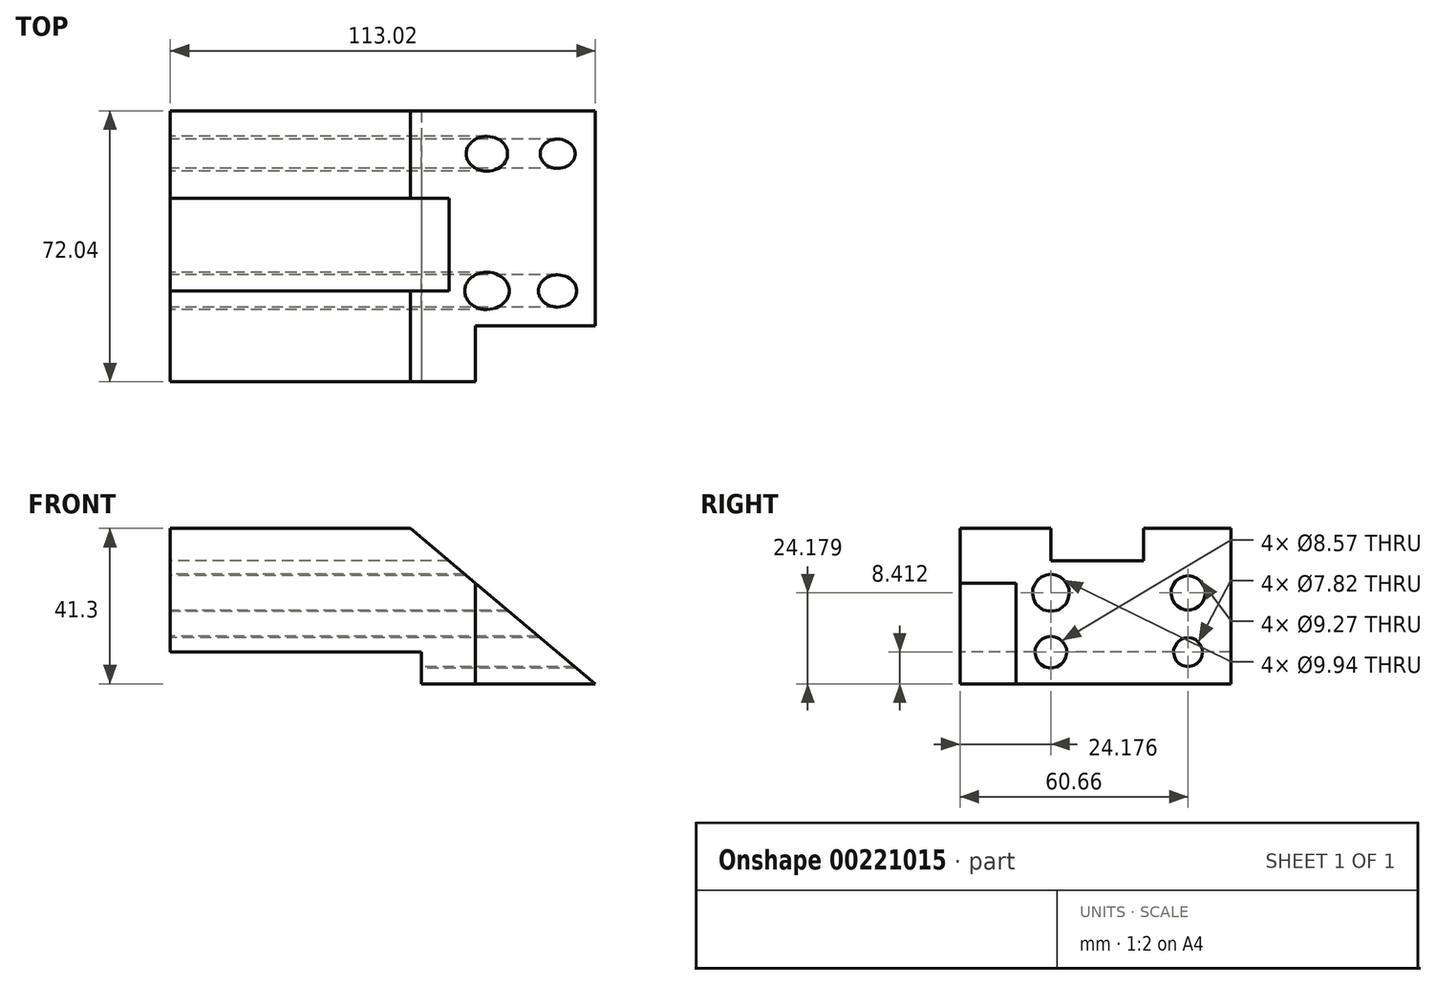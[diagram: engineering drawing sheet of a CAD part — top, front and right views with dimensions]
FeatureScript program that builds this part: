
annotation { "Feature Type Name" : "Feature", "Feature Type Description" : "" }
export const myFeature = defineFeature(function(context is Context, id is Id, definition is map)
    precondition{}
    {
        {
            var Q0;
            Q0=qCreatedBy(makeId("Top.planeOp"),FACE);
            var sketch = newSketch(context, id + "F0", { "sketchPlane" : qUnion([Q0])});
            skLineSegment(sketch, "E0.bottom", {"start": v(57.3, -36.02) * mm, "end": v(-57.3, -36.02) * mm});
            skLineSegment(sketch, "E0.top", {"start": v(57.3, 36.02) * mm, "end": v(-57.3, 36.02) * mm});
            skLineSegment(sketch, "E0.left", {"start": v(57.3, -36.02) * mm, "end": v(57.3, 36.02) * mm});
            skLineSegment(sketch, "E0.right", {"start": v(-57.3, -36.02) * mm, "end": v(-57.3, 36.02) * mm});
            skPoint(sketch, "E0.middle", {"position": v(0, 0) * mm});
            skSolve(sketch);
        }
        {
            var Q0;
            Q0 = qSketchRegion(id + "F0", true);
            extrude(context, id + "F1", {"entities" : qUnion([Q0]), "depth" : 41.3 * mm});
        }
        {
            var Q0;
            Q0=makeQuery(id+"F1.opExtrude","SWEPT_FACE",FACE,{"disambiguationData":[OSD([sQuery(id+"F0.wireOp",EDGE,"E0.bottom")])]});
            var sketch = newSketch(context, id + "F2", { "sketchPlane" : qUnion([Q0])});
            skLineSegment(sketch, "E1.bottom", {"start": v(-57.3, 0) * mm, "end": v(-57.3, 0) * mm});
            skLineSegment(sketch, "E1.top", {"start": v(-57.3, 0) * mm, "end": v(-57.3, 0) * mm});
            skLineSegment(sketch, "E1.left", {"start": v(-57.3, 0) * mm, "end": v(-57.3, 0) * mm});
            skLineSegment(sketch, "E1.right", {"start": v(-57.3, 0) * mm, "end": v(-57.3, 0) * mm});
            skLineSegment(sketch, "E2.bottom", {"start": v(-57.3, 0) * mm, "end": v(9.51, 0) * mm});
            skLineSegment(sketch, "E2.top", {"start": v(-57.3, 8.41) * mm, "end": v(9.51, 8.41) * mm});
            skLineSegment(sketch, "E2.left", {"start": v(-57.3, 0) * mm, "end": v(-57.3, 8.41) * mm});
            skLineSegment(sketch, "E2.right", {"start": v(9.51, 0) * mm, "end": v(9.51, 8.41) * mm});
            skSolve(sketch);
        }
        {
            var Q0;
            Q0 = qSketchRegion(id + "F2", true);
            var Q1;
            Q1=makeQuery(id+"F2.imprint","IMPRINT",FACE,{"disambiguationData":[TD([[makeQuery(id+"F2.imprint","IMPRINT",EDGE,{"derivedFrom":sQuery(id+"F2.wireOp",EDGE,"E2.bottom")}),-1.0]])]});
            extrude(context, id + "F6", {"entities" : qUnion([Q0, Q1]), "operationType" : NewBodyOperationType.REMOVE, "endBound" : BoundingType.THROUGH_ALL, "oppositeDirection" : true, "depth" : 25.4 * mm});
        }
        {
            var Q0;
            Q0=makeQuery(id+"F1.opExtrude","CAP_EDGE",EDGE,{"disambiguationData":[OSD([sQuery(id+"F0.wireOp",EDGE,"E0.left")])],"isStart":false});
            chamfer(context, id + "F7", {"entities" : qUnion([Q0]), "chamferType" : ChamferType.OFFSET_ANGLE, "width" : 50.8 * mm, "oppositeDirection" : false, "angle" : 40 * degree, "tangentPropagation" : true});
        }
        {
            var Q0;
            Q0=makeQuery(id+"F1.opExtrude","CAP_FACE",FACE,{"disambiguationData":[OSD([sQuery(id+"F0.wireOp",EDGE,"E0.bottom"),sQuery(id+"F0.wireOp",EDGE,"E0.top"),sQuery(id+"F0.wireOp",EDGE,"E0.left"),sQuery(id+"F0.wireOp",EDGE,"E0.right")])],"isStart":true});
            var sketch = newSketch(context, id + "F3", { "sketchPlane" : qUnion([Q0])});
            skLineSegment(sketch, "E3.bottom", {"start": v(55.72, 36.02) * mm, "end": v(23.82, 36.02) * mm});
            skLineSegment(sketch, "E3.top", {"start": v(55.72, 21.18) * mm, "end": v(23.82, 21.18) * mm});
            skLineSegment(sketch, "E3.left", {"start": v(55.72, 36.02) * mm, "end": v(55.72, 21.18) * mm});
            skLineSegment(sketch, "E3.right", {"start": v(23.82, 36.02) * mm, "end": v(23.82, 21.18) * mm});
            skSolve(sketch);
        }
        {
            var Q0;
            Q0=makeQuery(id+"F3.imprint","IMPRINT",FACE,{"disambiguationData":[TD([[makeQuery(id+"F3.imprint","IMPRINT",EDGE,{"derivedFrom":sQuery(id+"F3.wireOp",EDGE,"E3.bottom")}),1.0]])]});
            extrude(context, id + "F4", {"entities" : qUnion([Q0]), "operationType" : NewBodyOperationType.REMOVE, "endBound" : BoundingType.THROUGH_ALL, "oppositeDirection" : true, "depth" : 25.4 * mm});
        }
        {
            var Q0;
            Q0=makeQuery(id+"F1.opExtrude","SWEPT_FACE",FACE,{"disambiguationData":[OSD([sQuery(id+"F0.wireOp",EDGE,"E0.right")])]});
            var sketch = newSketch(context, id + "F5", { "sketchPlane" : qUnion([Q0])});
            skLineSegment(sketch, "E4.bottom", {"start": v(-12.81, 41.3) * mm, "end": v(11.84, 41.3) * mm});
            skLineSegment(sketch, "E4.top", {"start": v(-12.81, 32.67) * mm, "end": v(11.84, 32.67) * mm});
            skLineSegment(sketch, "E4.left", {"start": v(-12.81, 41.3) * mm, "end": v(-12.81, 32.67) * mm});
            skLineSegment(sketch, "E4.right", {"start": v(11.84, 41.3) * mm, "end": v(11.84, 32.67) * mm});
            skSolve(sketch);
        }
        {
            var Q0;
            Q0=makeQuery(id+"F5.imprint","IMPRINT",FACE,{"disambiguationData":[TD([[makeQuery(id+"F5.imprint","IMPRINT",EDGE,{"derivedFrom":sQuery(id+"F5.wireOp",EDGE,"E4.bottom")}),1.0]])]});
            extrude(context, id + "F8", {"entities" : qUnion([Q0]), "operationType" : NewBodyOperationType.REMOVE, "endBound" : BoundingType.THROUGH_ALL, "oppositeDirection" : true, "depth" : 25.4 * mm});
        }
        {
            var Q0;
            Q0=makeQuery(id+"F1.opExtrude","SWEPT_FACE",FACE,{"disambiguationData":[OSD([sQuery(id+"F0.wireOp",EDGE,"E0.right")])]});
            var sketch = newSketch(context, id + "F9", { "sketchPlane" : qUnion([Q0])});
            skCircle(sketch, "E5", {"center": v(-24.64, 24.18) * mm, "radius": 4.63 * mm});
            skCircle(sketch, "E6", {"center": v(11.84, 24.18) * mm, "radius": 4.97 * mm});
            skCircle(sketch, "E7", {"center": v(-24.64, 8.41) * mm, "radius": 3.91 * mm});
            skCircle(sketch, "E8", {"center": v(11.84, 8.41) * mm, "radius": 4.28 * mm});
            skSolve(sketch);
        }
        {
            var Q0;
            Q0=makeQuery(id+"F9.imprint","IMPRINT",FACE,{"disambiguationData":[TD([[makeQuery(id+"F9.imprint","IMPRINT",EDGE,{"derivedFrom":sQuery(id+"F9.wireOp",EDGE,"E5")}),1.0]])]});
            var Q1;
            Q1=makeQuery(id+"F9.imprint","IMPRINT",FACE,{"disambiguationData":[TD([[makeQuery(id+"F9.imprint","IMPRINT",EDGE,{"derivedFrom":sQuery(id+"F9.wireOp",EDGE,"E6")}),1.0]])]});
            var Q2;
            {var subQ0=sQuery(id+"F9.wireOp",EDGE,"E8");var subQ1=makeQuery(id+"F6.boolean.opBoolean","COPY",EDGE,{"derivedFrom":makeQuery(id+"F6.opExtrude","SWEPT_EDGE",EDGE,{"disambiguationData":[OSD([sQuery(id+"F0.wireOp",EDGE,"E0.bottom"),sQuery(id+"F0.wireOp",EDGE,"E0.right"),sQuery(id+"F2.wireOp",EDGE,"E2.top"),sQuery(id+"F2.wireOp",EDGE,"E2.left")])]})});var subQ2=makeQuery(id+"F9.imprint","INTERSECT",VERTEX,{"disambiguationData":[OD(0.0)],"derivedFrom":[subQ1,subQ0]});Q2=makeQuery(id+"F9.imprint","IMPRINT",FACE,{"disambiguationData":[TD([[makeQuery(id+"F9.imprint","IMPRINT",EDGE,{"disambiguationData":[TD([[subQ2,1.0]])],"derivedFrom":subQ0}),1.0]])]});}
            var Q3;
            {var subQ0=sQuery(id+"F9.wireOp",EDGE,"E7");var subQ1=makeQuery(id+"F6.boolean.opBoolean","COPY",EDGE,{"derivedFrom":makeQuery(id+"F6.opExtrude","SWEPT_EDGE",EDGE,{"disambiguationData":[OSD([sQuery(id+"F0.wireOp",EDGE,"E0.bottom"),sQuery(id+"F0.wireOp",EDGE,"E0.right"),sQuery(id+"F2.wireOp",EDGE,"E2.top"),sQuery(id+"F2.wireOp",EDGE,"E2.left")])]})});var subQ2=makeQuery(id+"F9.imprint","INTERSECT",VERTEX,{"disambiguationData":[OD(0.0)],"derivedFrom":[subQ1,subQ0]});Q3=makeQuery(id+"F9.imprint","IMPRINT",FACE,{"disambiguationData":[TD([[makeQuery(id+"F9.imprint","IMPRINT",EDGE,{"disambiguationData":[TD([[subQ2,-1.0]])],"derivedFrom":subQ0}),1.0]])]});}
            var Q4;
            {var subQ0=sQuery(id+"F9.wireOp",EDGE,"E7");var subQ1=makeQuery(id+"F6.boolean.opBoolean","COPY",EDGE,{"derivedFrom":makeQuery(id+"F6.opExtrude","SWEPT_EDGE",EDGE,{"disambiguationData":[OSD([sQuery(id+"F0.wireOp",EDGE,"E0.bottom"),sQuery(id+"F0.wireOp",EDGE,"E0.right"),sQuery(id+"F2.wireOp",EDGE,"E2.top"),sQuery(id+"F2.wireOp",EDGE,"E2.left")])]})});var subQ2=makeQuery(id+"F9.imprint","INTERSECT",VERTEX,{"disambiguationData":[OD(0.0)],"derivedFrom":[subQ1,subQ0]});Q4=makeQuery(id+"F9.imprint","IMPRINT",FACE,{"disambiguationData":[TD([[makeQuery(id+"F9.imprint","IMPRINT",EDGE,{"disambiguationData":[TD([[subQ2,1.0]])],"derivedFrom":subQ0}),1.0]])]});}
            var Q5;
            {var subQ0=sQuery(id+"F9.wireOp",EDGE,"E8");var subQ1=makeQuery(id+"F6.boolean.opBoolean","COPY",EDGE,{"derivedFrom":makeQuery(id+"F6.opExtrude","SWEPT_EDGE",EDGE,{"disambiguationData":[OSD([sQuery(id+"F0.wireOp",EDGE,"E0.bottom"),sQuery(id+"F0.wireOp",EDGE,"E0.right"),sQuery(id+"F2.wireOp",EDGE,"E2.top"),sQuery(id+"F2.wireOp",EDGE,"E2.left")])]})});var subQ2=makeQuery(id+"F9.imprint","INTERSECT",VERTEX,{"disambiguationData":[OD(0.0)],"derivedFrom":[subQ1,subQ0]});Q5=makeQuery(id+"F9.imprint","IMPRINT",FACE,{"disambiguationData":[TD([[makeQuery(id+"F9.imprint","IMPRINT",EDGE,{"disambiguationData":[TD([[subQ2,-1.0]])],"derivedFrom":subQ0}),1.0]])]});}
            extrude(context, id + "F10", {"entities" : qUnion([Q0, Q1, Q2, Q3, Q4, Q5]), "operationType" : NewBodyOperationType.REMOVE, "endBound" : BoundingType.THROUGH_ALL, "oppositeDirection" : true, "depth" : 25.4 * mm});
        }
    });
